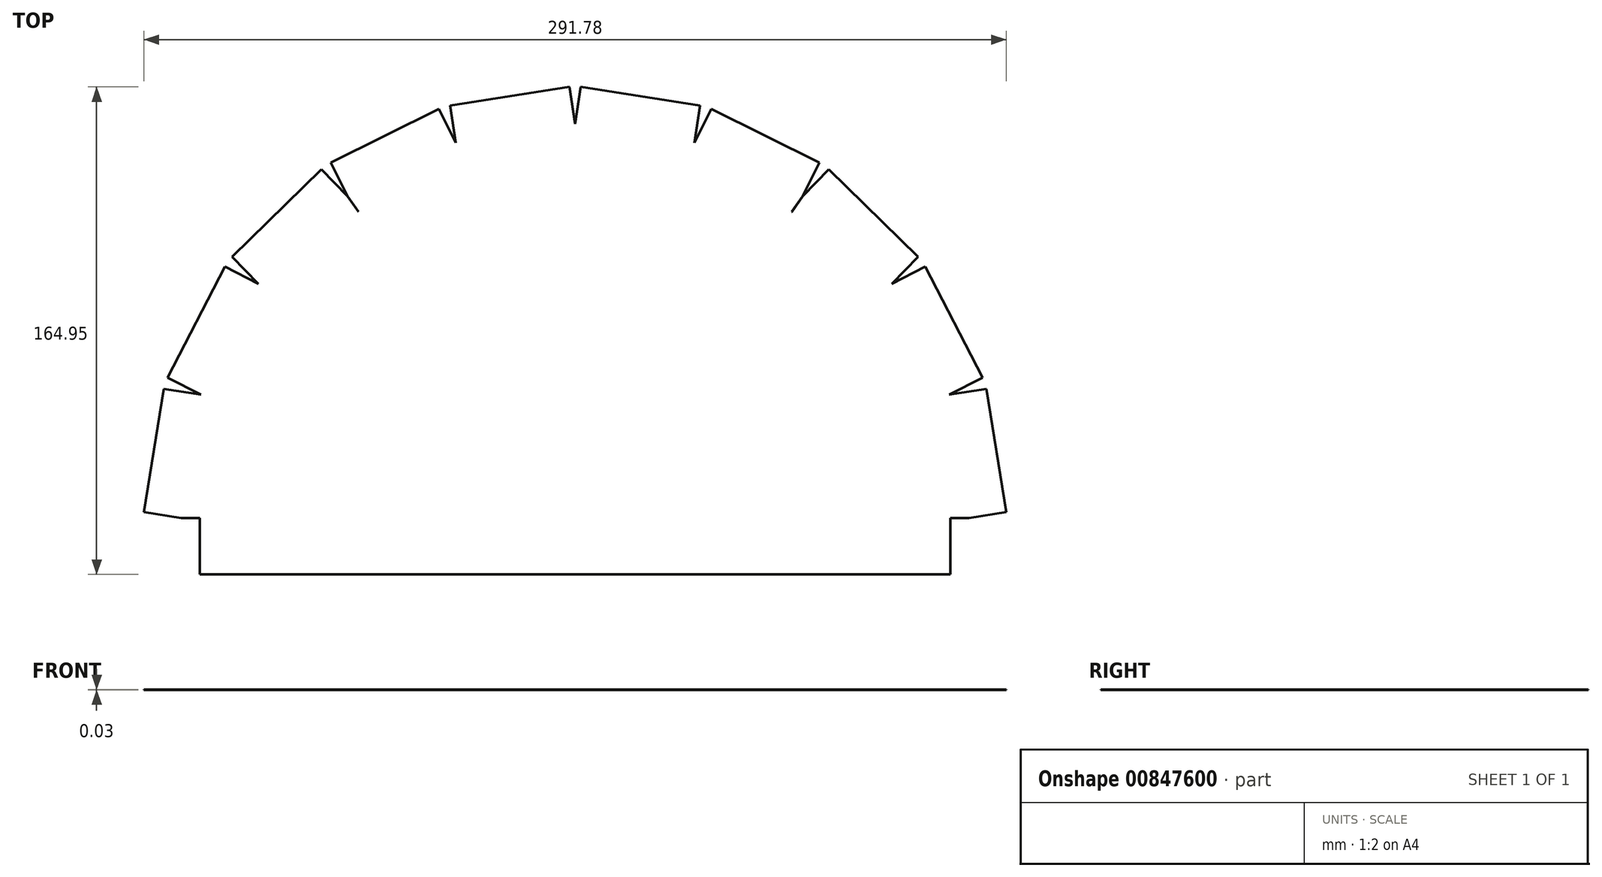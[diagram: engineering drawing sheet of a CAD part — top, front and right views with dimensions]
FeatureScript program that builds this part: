
annotation { "Feature Type Name" : "Feature", "Feature Type Description" : "" }
export const myFeature = defineFeature(function(context is Context, id is Id, definition is map)
    precondition{}
    {
        {
            var Q0;
            Q0=qCreatedBy(makeId("Top.planeOp"),FACE);
            var sketch = newSketch(context, id + "F0", { "sketchPlane" : qUnion([Q0])});
            skLineSegment(sketch, "E0", {"start": v(127, 0) * mm, "end": v(-127, 0) * mm, "construction": true});
            skArc(sketch, "E1", {"start": v(-127, 0) * mm, "mid": v(-112.79, 58.38) * mm, "end": v(-73.34, 103.69) * mm, "construction": true});
            skArc(sketch, "E2", {"start": v(127, 0) * mm, "mid": v(112.79, 58.38) * mm, "end": v(73.34, 103.69) * mm, "construction": true});
            skArc(sketch, "E3", {"start": v(-73.34, 103.69) * mm, "mid": v(0, 127) * mm, "end": v(73.34, 103.69) * mm, "construction": true});
            skLineSegment(sketch, "E4", {"start": v(127, 0) * mm, "end": v(127, -19.05) * mm});
            skLineSegment(sketch, "E5", {"start": v(127, -19.05) * mm, "end": v(-127, -19.05) * mm});
            skLineSegment(sketch, "E6", {"start": v(-127, -19.05) * mm, "end": v(-127, 0) * mm});
            skArc(sketch, "E7", {"start": v(133.35, 0) * mm, "mid": v(118.43, 61.3) * mm, "end": v(77, 108.88) * mm, "construction": true});
            skArc(sketch, "E8", {"start": v(-77, 108.88) * mm, "mid": v(-118.43, 61.3) * mm, "end": v(-133.35, 0) * mm, "construction": true});
            skLineSegment(sketch, "E9", {"start": v(-127, 0) * mm, "end": v(-133.35, 0) * mm});
            skLineSegment(sketch, "E10", {"start": v(127, 0) * mm, "end": v(133.35, 0) * mm});
            skLineSegment(sketch, "E11", {"start": v(-73.35, 103.68) * mm, "end": v(-73.33, 103.7) * mm});
            skLineSegment(sketch, "E12", {"start": v(-73.33, 103.7) * mm, "end": v(-77, 108.88) * mm});
            skLineSegment(sketch, "E13", {"start": v(-73.35, 103.68) * mm, "end": v(-77.1, 109) * mm});
            skLineSegment(sketch, "E14", {"start": v(77.1, 109) * mm, "end": v(73.35, 103.68) * mm});
            skLineSegment(sketch, "E15", {"start": v(73.35, 103.68) * mm, "end": v(73.33, 103.7) * mm});
            skLineSegment(sketch, "E16", {"start": v(73.33, 103.7) * mm, "end": v(77, 108.88) * mm});
            skPoint(sketch, "E17", {"position": v(-73.34, 103.69) * mm});
            skPoint(sketch, "E18", {"position": v(73.34, 103.69) * mm});
            skArc(sketch, "E19", {"start": v(-77, 108.88) * mm, "mid": v(0, 133.35) * mm, "end": v(77, 108.88) * mm, "construction": true});
            skLineSegment(sketch, "E20", {"start": v(-133.35, 0) * mm, "end": v(-126.65, 41.75) * mm, "construction": true});
            skLineSegment(sketch, "E21", {"start": v(-126.65, 41.75) * mm, "end": v(-139.19, 43.76) * mm});
            skLineSegment(sketch, "E22", {"start": v(-139.19, 43.76) * mm, "end": v(-145.89, 2.01) * mm});
            skLineSegment(sketch, "E23", {"start": v(-145.89, 2.01) * mm, "end": v(-133.35, 0) * mm});
            skLineSegment(sketch, "E24", {"start": v(-126.65, 41.75) * mm, "end": v(-137.92, 47.59) * mm});
            skLineSegment(sketch, "E25", {"start": v(-137.92, 47.59) * mm, "end": v(-118.49, 85.14) * mm});
            skLineSegment(sketch, "E26", {"start": v(-118.49, 85.14) * mm, "end": v(-107.2, 79.3) * mm});
            skLineSegment(sketch, "E27", {"start": v(-107.2, 79.3) * mm, "end": v(-126.65, 41.75) * mm, "construction": true});
            skLineSegment(sketch, "E28", {"start": v(-107.2, 79.3) * mm, "end": v(-77, 108.88) * mm, "construction": true});
            skLineSegment(sketch, "E29", {"start": v(-107.2, 79.3) * mm, "end": v(-116.1, 88.38) * mm});
            skLineSegment(sketch, "E30", {"start": v(-116.1, 88.38) * mm, "end": v(-85.88, 117.95) * mm});
            skLineSegment(sketch, "E31", {"start": v(-85.88, 117.95) * mm, "end": v(-77, 108.88) * mm, "construction": true});
            skLineSegment(sketch, "E32", {"start": v(-40.4, 127.08) * mm, "end": v(-77, 108.88) * mm, "construction": true});
            skLineSegment(sketch, "E33", {"start": v(-40.4, 127.08) * mm, "end": v(-42.34, 139.63) * mm});
            skLineSegment(sketch, "E34", {"start": v(-42.34, 139.63) * mm, "end": v(-1.95, 145.9) * mm});
            skLineSegment(sketch, "E35", {"start": v(-1.95, 145.9) * mm, "end": v(0, 133.35) * mm});
            skLineSegment(sketch, "E36", {"start": v(0, 133.35) * mm, "end": v(-40.4, 127.08) * mm, "construction": true});
            skLineSegment(sketch, "E37", {"start": v(-40.4, 127.08) * mm, "end": v(-46.05, 138.46) * mm});
            skLineSegment(sketch, "E38", {"start": v(-46.05, 138.46) * mm, "end": v(-82.65, 120.25) * mm});
            skLineSegment(sketch, "E39", {"start": v(-82.65, 120.25) * mm, "end": v(-77, 108.88) * mm});
            skLineSegment(sketch, "E40.MirrorCS", {"start": v(145.89, 2.01) * mm, "end": v(133.35, 0) * mm});
            skLineSegment(sketch, "E41.MirrorCS", {"start": v(139.19, 43.76) * mm, "end": v(145.89, 2.01) * mm});
            skLineSegment(sketch, "E42.MirrorCS", {"start": v(126.65, 41.75) * mm, "end": v(139.19, 43.76) * mm});
            skLineSegment(sketch, "E43.MirrorCS", {"start": v(133.35, 0) * mm, "end": v(126.65, 41.75) * mm, "construction": true});
            skLineSegment(sketch, "E44.MirrorCS", {"start": v(126.65, 41.75) * mm, "end": v(137.92, 47.59) * mm});
            skLineSegment(sketch, "E45.MirrorCS", {"start": v(137.92, 47.59) * mm, "end": v(118.49, 85.14) * mm});
            skLineSegment(sketch, "E46.MirrorCS", {"start": v(118.49, 85.14) * mm, "end": v(107.2, 79.3) * mm});
            skLineSegment(sketch, "E47.MirrorCS", {"start": v(107.2, 79.3) * mm, "end": v(126.65, 41.75) * mm, "construction": true});
            skLineSegment(sketch, "E48.MirrorCS", {"start": v(107.2, 79.3) * mm, "end": v(116.1, 88.38) * mm});
            skLineSegment(sketch, "E49.MirrorCS", {"start": v(107.2, 79.3) * mm, "end": v(77, 108.88) * mm, "construction": true});
            skLineSegment(sketch, "E50.MirrorCS", {"start": v(116.1, 88.38) * mm, "end": v(85.88, 117.95) * mm});
            skLineSegment(sketch, "E51.MirrorCS", {"start": v(85.88, 117.95) * mm, "end": v(77, 108.88) * mm, "construction": true});
            skLineSegment(sketch, "E52.MirrorCS", {"start": v(82.65, 120.25) * mm, "end": v(77, 108.88) * mm});
            skLineSegment(sketch, "E53.MirrorCS", {"start": v(46.05, 138.46) * mm, "end": v(82.65, 120.25) * mm});
            skLineSegment(sketch, "E54.MirrorCS", {"start": v(40.4, 127.08) * mm, "end": v(46.05, 138.46) * mm});
            skLineSegment(sketch, "E55.MirrorCS", {"start": v(40.4, 127.08) * mm, "end": v(77, 108.88) * mm, "construction": true});
            skLineSegment(sketch, "E56.MirrorCS", {"start": v(40.4, 127.08) * mm, "end": v(42.34, 139.63) * mm});
            skLineSegment(sketch, "E57.MirrorCS", {"start": v(0, 133.35) * mm, "end": v(40.4, 127.08) * mm, "construction": true});
            skLineSegment(sketch, "E58.MirrorCS", {"start": v(1.95, 145.9) * mm, "end": v(0, 133.35) * mm});
            skLineSegment(sketch, "E59.MirrorCS", {"start": v(42.34, 139.63) * mm, "end": v(1.95, 145.9) * mm});
            skLineSegment(sketch, "E60", {"start": v(-77.1, 109) * mm, "end": v(-85.88, 117.95) * mm});
            skLineSegment(sketch, "E61", {"start": v(77.1, 109) * mm, "end": v(85.88, 117.95) * mm});
            skSolve(sketch);
        }
        {
            var Q0;
            Q0 = qSketchRegion(id + "F0", true);
            extrude(context, id + "F1", {"entities" : qUnion([Q0]), "depth" : 0.03 * mm, "offsetDistance" : 25.4 * mm});
        }
    });
